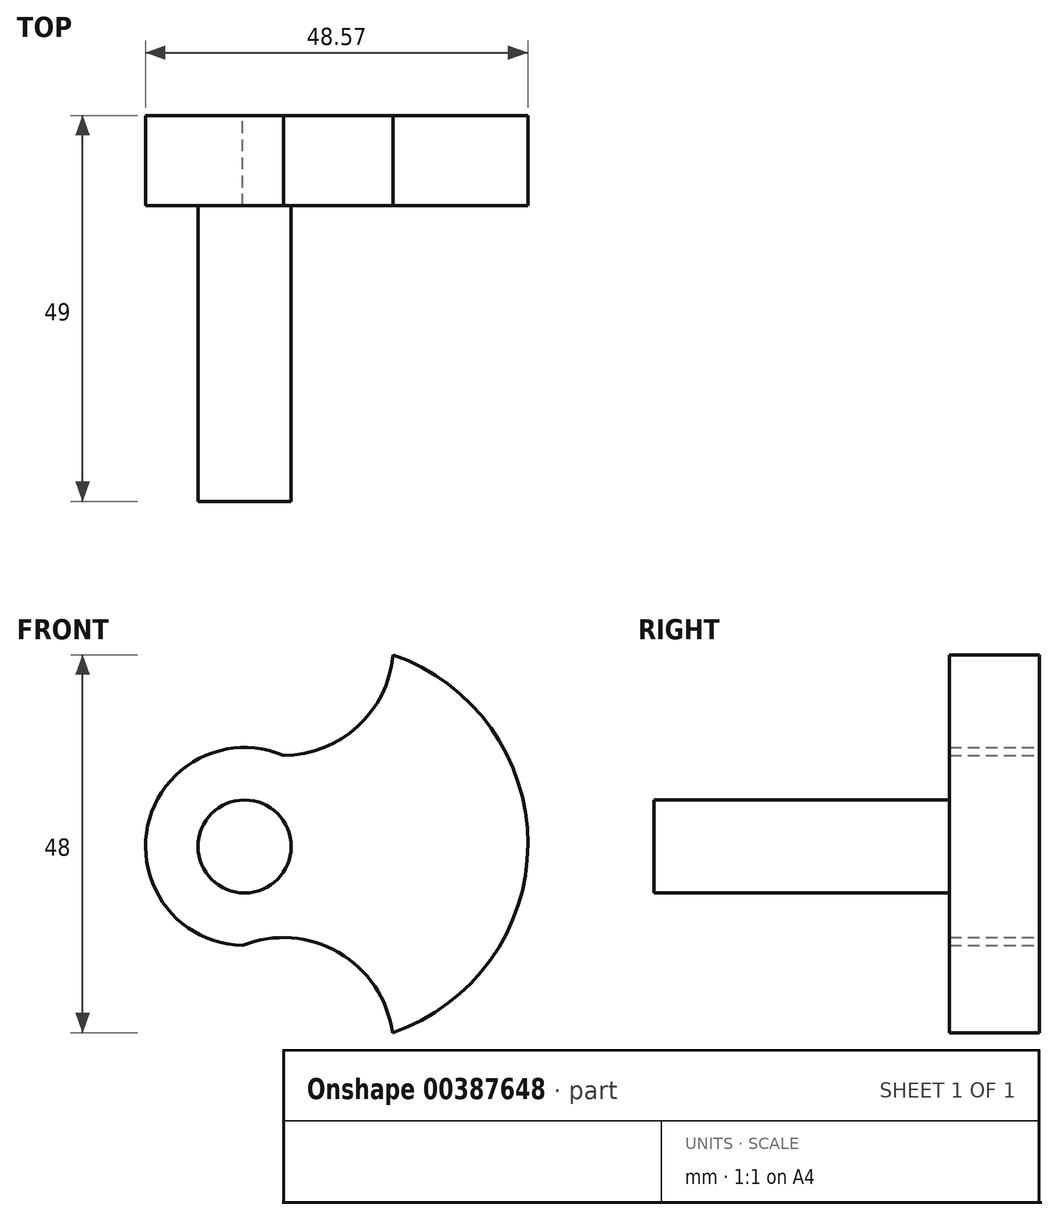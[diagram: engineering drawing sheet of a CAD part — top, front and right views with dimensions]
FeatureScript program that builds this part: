
annotation { "Feature Type Name" : "Feature", "Feature Type Description" : "" }
export const myFeature = defineFeature(function(context is Context, id is Id, definition is map)
    precondition{}
    {
        {
            var Q0;
            Q0=qCreatedBy(makeId("Front.planeOp"),FACE);
            var sketch = newSketch(context, id + "F0", { "sketchPlane" : qUnion([Q0])});
            skArc(sketch, "E0", {"start": v(13.86, -21.9) * mm, "mid": v(7.03, -11.73) * mm, "end": v(-5.2, -10.83) * mm});
            skArc(sketch, "E1", {"start": v(0, 13.32) * mm, "mid": v(9.45, 17) * mm, "end": v(13.94, 26.09) * mm});
            skPoint(sketch, "E2", {"position": v(-17.38, 0) * mm});
            skPoint(sketch, "E3", {"position": v(0, 13.32) * mm});
            skPoint(sketch, "E4", {"position": v(0, -9.83) * mm});
            skPoint(sketch, "E5", {"position": v(13.94, 26.09) * mm});
            skPoint(sketch, "E6", {"position": v(13.86, -21.9) * mm});
            skArc(sketch, "E7", {"start": v(0, 13.32) * mm, "mid": v(-17.22, 4.39) * mm, "end": v(-5.2, -10.83) * mm});
            skCircle(sketch, "E8", {"center": v(-4.92, 1.74) * mm, "radius": 5.9 * mm});
            skArc(sketch, "E9", {"start": v(13.86, -21.9) * mm, "mid": v(31.07, 2.06) * mm, "end": v(13.94, 26.09) * mm});
            skPoint(sketch, "E10", {"position": v(31.07, 2.1) * mm});
            skSolve(sketch);
        }
        {
            var Q0;
            Q0=makeQuery(id+"F0.imprint","IMPRINT",FACE,{"disambiguationData":[TD([[makeQuery(id+"F0.imprint","IMPRINT",EDGE,{"derivedFrom":sQuery(id+"F0.wireOp",EDGE,"E0")}),-1.0]])]});
            extrude(context, id + "F1", {"entities" : qUnion([Q0]), "depth" : 11.43 * mm});
        }
        {
            var Q0;
            Q0=makeQuery(id+"F0.imprint","IMPRINT",FACE,{"disambiguationData":[TD([[makeQuery(id+"F0.imprint","IMPRINT",EDGE,{"derivedFrom":sQuery(id+"F0.wireOp",EDGE,"E8")}),1.0]])]});
            extrude(context, id + "F2", {"entities" : qUnion([Q0]), "operationType" : NewBodyOperationType.ADD, "depth" : 49 * mm});
        }
    });
